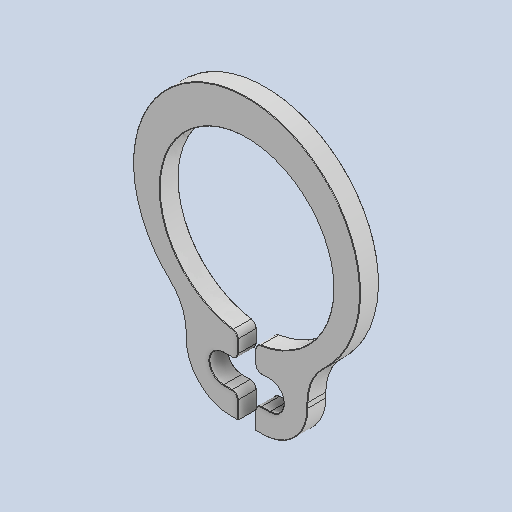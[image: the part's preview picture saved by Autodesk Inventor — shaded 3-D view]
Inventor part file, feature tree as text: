
AUTODESK INVENTOR PART (.ipt)
format: ipt  version: 2025 (Build 290162000, 162)  size: 196,608 bytes
history: native  units: in
note: dims shown in document units (in); Inventor stores cm internally (conversion verified against a paired STEP export)
features: fillet x1
ambient origin geometry x8: Origin, YZ Plane, XZ Plane, XY Plane, X Axis, Y Axis, Z Axis, Center Point
bodies: Solid1 (feature_tree)
feature tree (1):
  fillet  "Fillet1"  [1 undecoded]
note: 1 required parameter value undecoded (feature->parameter linkage not recoverable at this tier; creation-order binding heuristic only, values carry confidence <= 0.55)
